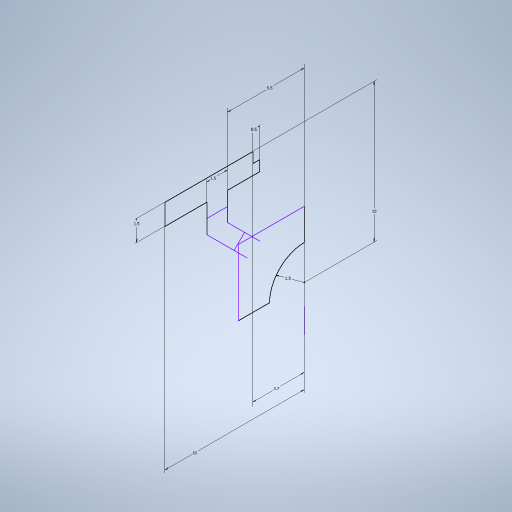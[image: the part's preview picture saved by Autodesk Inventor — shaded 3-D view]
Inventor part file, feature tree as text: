
AUTODESK INVENTOR PART (.ipt)
format: ipt  version: 2023 (Build 270158000, 158)  size: 246,784 bytes
history: native  units: mm
features: sketch x1
ambient origin geometry x8: Origin, YZ Plane, XZ Plane, XY Plane, X Axis, Y Axis, Z Axis, Center Point
feature tree (1):
  sketch  "Sketch1"  dims[d1=0.5mm d2=10.0mm d3=5.5mm d4=3.7mm d5=2.5mm d8=10.0mm d9=1.5mm d10=1.5mm]
